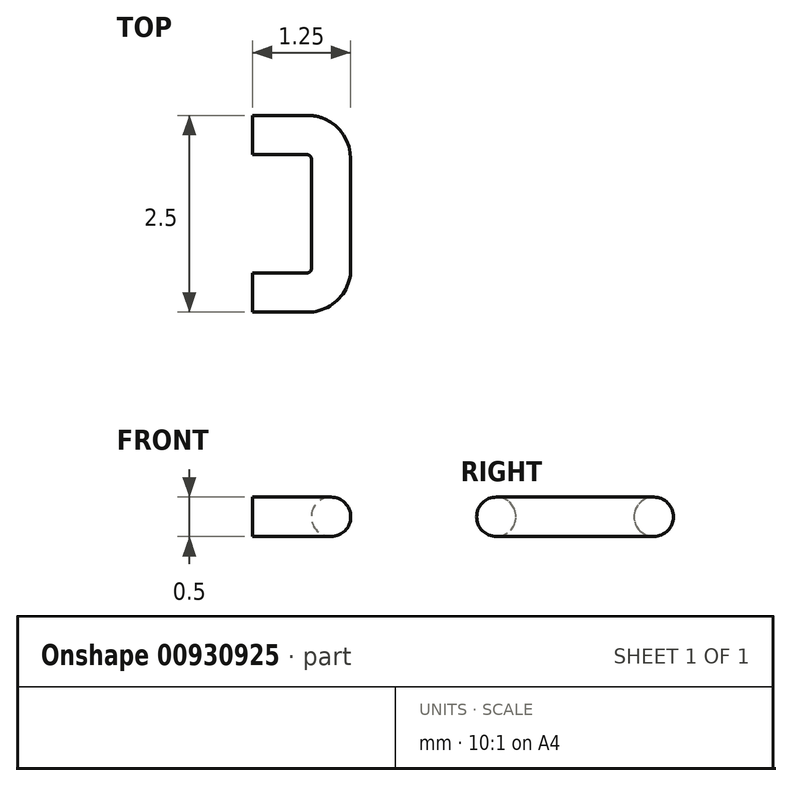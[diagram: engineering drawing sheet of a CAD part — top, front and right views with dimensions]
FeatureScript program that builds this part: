
annotation { "Feature Type Name" : "Feature", "Feature Type Description" : "" }
export const myFeature = defineFeature(function(context is Context, id is Id, definition is map)
    precondition{}
    {
        {
            var Q0;
            Q0=qCreatedBy(makeId("Right.planeOp"),FACE);
            var sketch = newSketch(context, id + "F0", { "sketchPlane" : qUnion([Q0])});
            skCircle(sketch, "E0", {"center": v(0, 0) * mm, "radius": 0.25 * mm});
            skSolve(sketch);
        }
        {
            var Q0;
            Q0=qCreatedBy(makeId("Top.planeOp"),FACE);
            var sketch = newSketch(context, id + "F1", { "sketchPlane" : qUnion([Q0])});
            skLineSegment(sketch, "E1", {"start": v(0, 0) * mm, "end": v(0.7, 0) * mm});
            skLineSegment(sketch, "E2", {"start": v(1, 0.3) * mm, "end": v(1, 1.7) * mm});
            skPoint(sketch, "E3.visualSharp", {"position": v(1, 0) * mm});
            skArc(sketch, "E3.filletArc", {"start": v(0.7, 0) * mm, "mid": v(0.91, 0.09) * mm, "end": v(1, 0.3) * mm});
            skLineSegment(sketch, "E4", {"start": v(0.7, 2) * mm, "end": v(0, 2) * mm});
            skPoint(sketch, "E5.visualSharp", {"position": v(1, 2) * mm});
            skArc(sketch, "E5.filletArc", {"start": v(1, 1.7) * mm, "mid": v(0.91, 1.91) * mm, "end": v(0.7, 2) * mm});
            skSolve(sketch);
        }
        {
            var Q0;
            Q0=qSketchRegion(id+"F0",true);
            var Q1;
            Q1=qBodyType(qCreatedBy(id+"F1",EDGE),BodyType.WIRE);
            sweep(context, id + "F2", {"profiles" : qUnion([Q0]), "path" : qUnion([Q1])});
        }
    });
